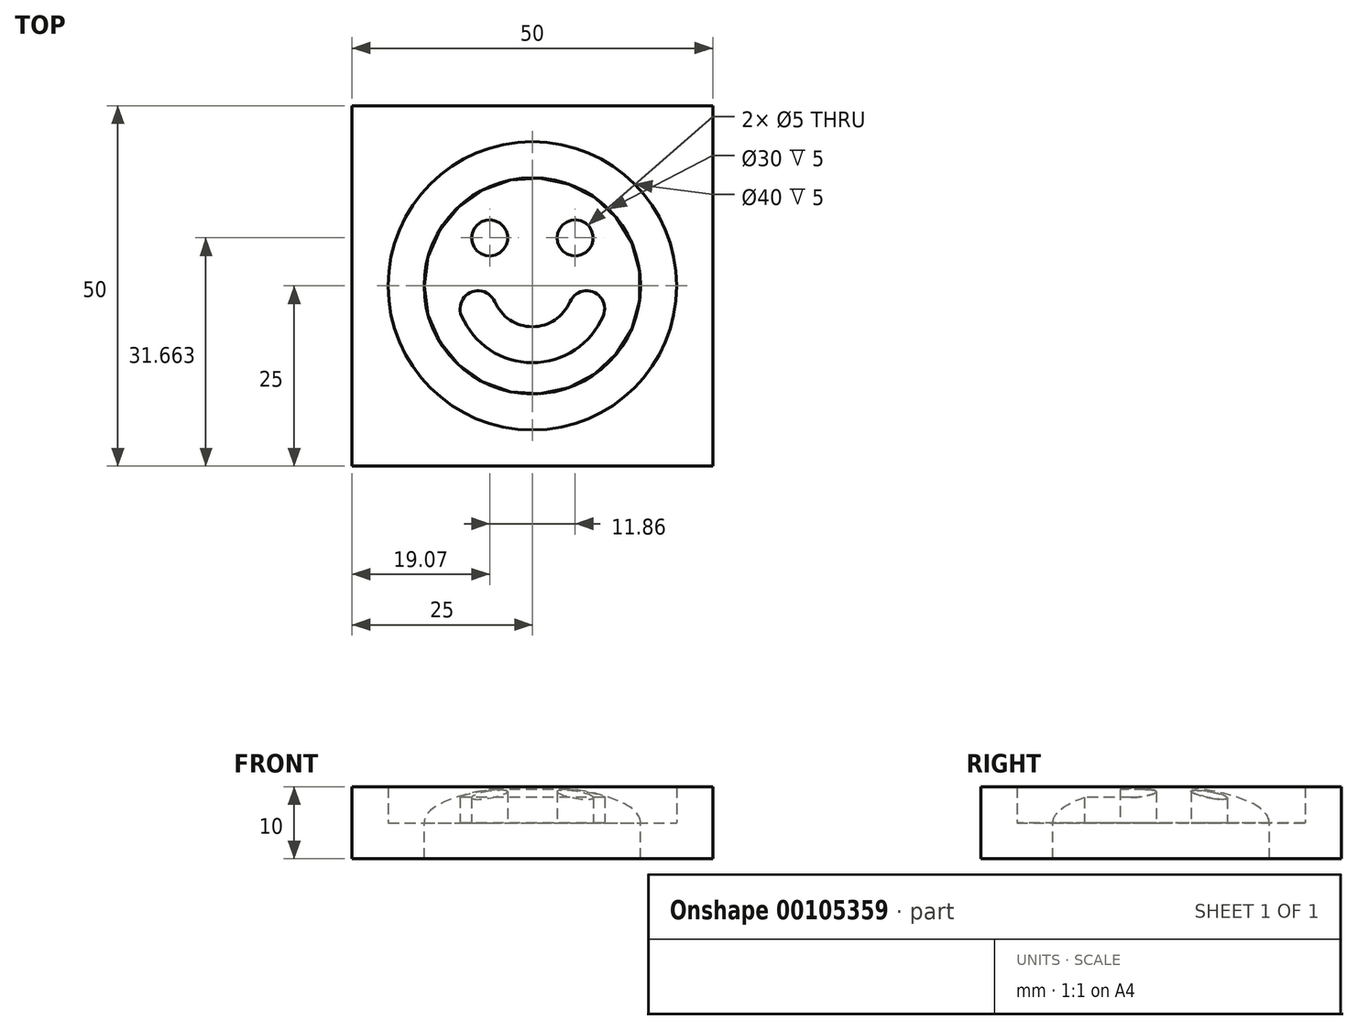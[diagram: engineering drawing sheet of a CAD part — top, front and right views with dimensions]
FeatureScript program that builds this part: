
annotation { "Feature Type Name" : "Feature", "Feature Type Description" : "" }
export const myFeature = defineFeature(function(context is Context, id is Id, definition is map)
    precondition{}
    {
        {
            var Q0;
            Q0=qCreatedBy(makeId("Front.planeOp"),FACE);
            var sketch = newSketch(context, id + "F0", { "sketchPlane" : qUnion([Q0])});
            skEllipticalArc(sketch, "E0", {});
            skLineSegment(sketch, "E1", {"start": v(0, 0) * mm, "end": v(0, 5) * mm});
            skLineSegment(sketch, "E2", {"start": v(0, 0) * mm, "end": v(-15, 0) * mm});
            const initialGuessF0  = {"E0": [0, 0, -1, 0, 0.015, 0.005, 4.71238898038469, 0]};
            skSetInitialGuess(sketch, initialGuessF0);
            skSolve(sketch);
        }
        {
            var Q0;
            Q0 = qSketchRegion(id + "F0", true);
            var Q1;
            Q1=sQuery(id+"F0.wireOp",EDGE,"E1");
            revolve(context, id + "F1", {"entities" : qUnion([Q0]), "axis" : qUnion([Q1]), "revolveType" : RevolveType.FULL});
        }
        {
            var Q0;
            Q0=makeQuery(id+"F1.opRevolve","SWEPT_FACE",FACE,{"disambiguationData":[OSD([sQuery(id+"F0.wireOp",EDGE,"E2")])]});
            var sketch = newSketch(context, id + "F2", { "sketchPlane" : qUnion([Q0])});
            skCircle(sketch, "E3", {"center": v(5.93, -6.66) * mm, "radius": 2.5 * mm});
            skArc(sketch, "E4", {"start": v(0, 5.66) * mm, "mid": v(3.13, 4.72) * mm, "end": v(5.21, 2.2) * mm});
            skArc(sketch, "E5", {"start": v(0, 10.66) * mm, "mid": v(5.9, 8.88) * mm, "end": v(9.82, 4.15) * mm});
            skLineSegment(sketch, "E6", {"start": v(9.82, 4.15) * mm, "end": v(0, 0) * mm, "construction": true});
            skArc(sketch, "E7", {"start": v(5.21, 2.2) * mm, "mid": v(8.49, 0.87) * mm, "end": v(9.82, 4.15) * mm});
            skCircle(sketch, "E8.MirrorC", {"center": v(-5.93, -6.66) * mm, "radius": 2.5 * mm});
            skArc(sketch, "E9.MirrorCS", {"start": v(0, 5.66) * mm, "mid": v(-3.13, 4.72) * mm, "end": v(-5.21, 2.2) * mm});
            skArc(sketch, "E10.MirrorCS", {"start": v(-5.21, 2.2) * mm, "mid": v(-8.49, 0.87) * mm, "end": v(-9.82, 4.15) * mm});
            skArc(sketch, "E11.MirrorCS", {"start": v(0, 10.66) * mm, "mid": v(-5.9, 8.88) * mm, "end": v(-9.82, 4.15) * mm});
            skSolve(sketch);
        }
        {
            var Q0;
            Q0 = qSketchRegion(id + "F2", true);
            extrude(context, id + "F3", {"entities" : qUnion([Q0]), "operationType" : NewBodyOperationType.REMOVE, "oppositeDirection" : true, "depth" : 25 * mm});
        }
        {
            var Q0;
            Q0=makeQuery(id+"F1.opRevolve","SWEPT_FACE",FACE,{"disambiguationData":[OSD([sQuery(id+"F0.wireOp",EDGE,"E2")])]});
            var sketch = newSketch(context, id + "F4", { "sketchPlane" : qUnion([Q0])});
            skCircle(sketch, "E12", {"center": v(0, 0) * mm, "radius": 20 * mm});
            skLineSegment(sketch, "E13", {"start": v(0, -25) * mm, "end": v(25, -25) * mm});
            skLineSegment(sketch, "E14", {"start": v(25, -25) * mm, "end": v(25, 0) * mm});
            skLineSegment(sketch, "E15.MirrorCS", {"start": v(0, -25) * mm, "end": v(-25, -25) * mm});
            skLineSegment(sketch, "E16.MirrorCS", {"start": v(-25, -25) * mm, "end": v(-25, 0) * mm});
            skLineSegment(sketch, "E17.MirrorCS", {"start": v(25, 25) * mm, "end": v(25, 0) * mm});
            skLineSegment(sketch, "E18.MirrorCS", {"start": v(0, 25) * mm, "end": v(25, 25) * mm});
            skLineSegment(sketch, "E19.MirrorCS", {"start": v(0, 25) * mm, "end": v(-25, 25) * mm});
            skLineSegment(sketch, "E20.MirrorCS", {"start": v(-25, 25) * mm, "end": v(-25, 0) * mm});
            skSolve(sketch);
        }
        {
            var Q0;
            Q0 = qSketchRegion(id + "F4", true);
            var Q1;
            Q1=makeQuery(id+"F4.imprint","IMPRINT",FACE,{"disambiguationData":[TD([[makeQuery(id+"F4.imprint","IMPRINT",EDGE,{"derivedFrom":makeQuery(id+"F3.boolean.opBoolean","COPY",EDGE,{"derivedFrom":makeQuery(id+"F3.opExtrude","CAP_EDGE",EDGE,{"disambiguationData":[OSD([sQuery(id+"F2.wireOp",EDGE,"E3")])],"isStart":true})})}),-1.0]])]});
            var Q2;
            Q2=makeQuery(id+"F4.imprint","IMPRINT",FACE,{"disambiguationData":[TD([[makeQuery(id+"F4.imprint","IMPRINT",EDGE,{"derivedFrom":sQuery(id+"F4.wireOp",EDGE,"E12")}),1.0]])]});
            var Q3;
            Q3=makeQuery(id+"F4.imprint","IMPRINT",FACE,{"disambiguationData":[TD([[makeQuery(id+"F4.imprint","IMPRINT",EDGE,{"derivedFrom":makeQuery(id+"F3.boolean.opBoolean","COPY",EDGE,{"derivedFrom":makeQuery(id+"F3.opExtrude","CAP_EDGE",EDGE,{"disambiguationData":[OSD([sQuery(id+"F2.wireOp",EDGE,"E7")])],"isStart":true})})}),1.0]])]});
            var Q4;
            Q4=makeQuery(id+"F4.imprint","IMPRINT",FACE,{"disambiguationData":[TD([[makeQuery(id+"F4.imprint","IMPRINT",EDGE,{"derivedFrom":makeQuery(id+"F3.boolean.opBoolean","COPY",EDGE,{"derivedFrom":makeQuery(id+"F3.opExtrude","CAP_EDGE",EDGE,{"disambiguationData":[OSD([sQuery(id+"F2.wireOp",EDGE,"E8.MirrorC")])],"isStart":true})})}),-1.0]])]});
            var Q5;
            Q5=makeQuery(id+"F4.imprint","IMPRINT",FACE,{"disambiguationData":[TD([[makeQuery(id+"F4.imprint","IMPRINT",EDGE,{"derivedFrom":makeQuery(id+"F3.boolean.opBoolean","COPY",EDGE,{"derivedFrom":makeQuery(id+"F3.opExtrude","CAP_EDGE",EDGE,{"disambiguationData":[OSD([sQuery(id+"F2.wireOp",EDGE,"E3")])],"isStart":true})})}),1.0]])]});
            extrude(context, id + "F5", {"entities" : qUnion([Q0, Q1, Q2, Q3, Q4, Q5]), "operationType" : NewBodyOperationType.ADD, "depth" : 5 * mm});
        }
        {
            var Q0;
            Q0=makeQuery(id+"F4.imprint","IMPRINT",FACE,{"disambiguationData":[TD([[makeQuery(id+"F4.imprint","IMPRINT",EDGE,{"derivedFrom":sQuery(id+"F4.wireOp",EDGE,"E12")}),-1.0]])]});
            extrude(context, id + "F6", {"entities" : qUnion([Q0]), "operationType" : NewBodyOperationType.ADD, "oppositeDirection" : true, "depth" : 5 * mm});
        }
    });
